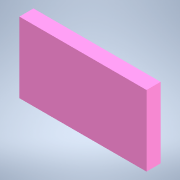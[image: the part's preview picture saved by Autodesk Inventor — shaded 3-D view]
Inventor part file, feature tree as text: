
AUTODESK INVENTOR PART (.ipt)
format: ipt  version: 2022.3 (Build 263350000, 350)  size: 97,792 bytes
history: native  units: in
note: dims shown in document units (in); Inventor stores cm internally (conversion verified against a paired STEP export)
features: extrude x1, sketch x1
ambient origin geometry x8: Origin, YZ Plane, XZ Plane, XY Plane, X Axis, Y Axis, Z Axis, Center Point
bodies: Solid1 (feature_tree)
feature tree (2):
  extrude  "Extrusion1"  Depth=4.5in
  sketch  "Sketch1"  dims[d0=0.5in d1=4.5in d2=2.5in d3=0.0in]
